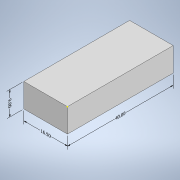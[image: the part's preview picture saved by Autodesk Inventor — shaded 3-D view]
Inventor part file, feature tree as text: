
AUTODESK INVENTOR PART (.ipt)
format: ipt  version: 2022 (Build 260153000, 153)  size: 102,912 bytes
history: native  units: mm
features: other x4, sketch x2, extrude x1
ambient origin geometry x8: Origin, YZ Plane, XZ Plane, XY Plane, X Axis, Y Axis, Z Axis, Center Point
bodies: Solid1 (feature_tree)
feature tree (7):
  other  "Annotations"
  extrude  "Extrusion1"  Depth=40.0mm
  sketch  "Sketch2"  dims[d2=9.0mm d3=0.0mm d10=0.0mm d11=10.0mm d12=9.0mm d4=0.0mm d5=10.0mm d6=16.5mm d7=0.0mm d8=10.0mm d9=40.0mm]
  sketch  "Sketch1"  dims[d0=16.5mm d1=40.0mm]
  other  "Linear Dimension 1"
  other  "Linear Dimension 2"
  other  "Linear Dimension 3"
